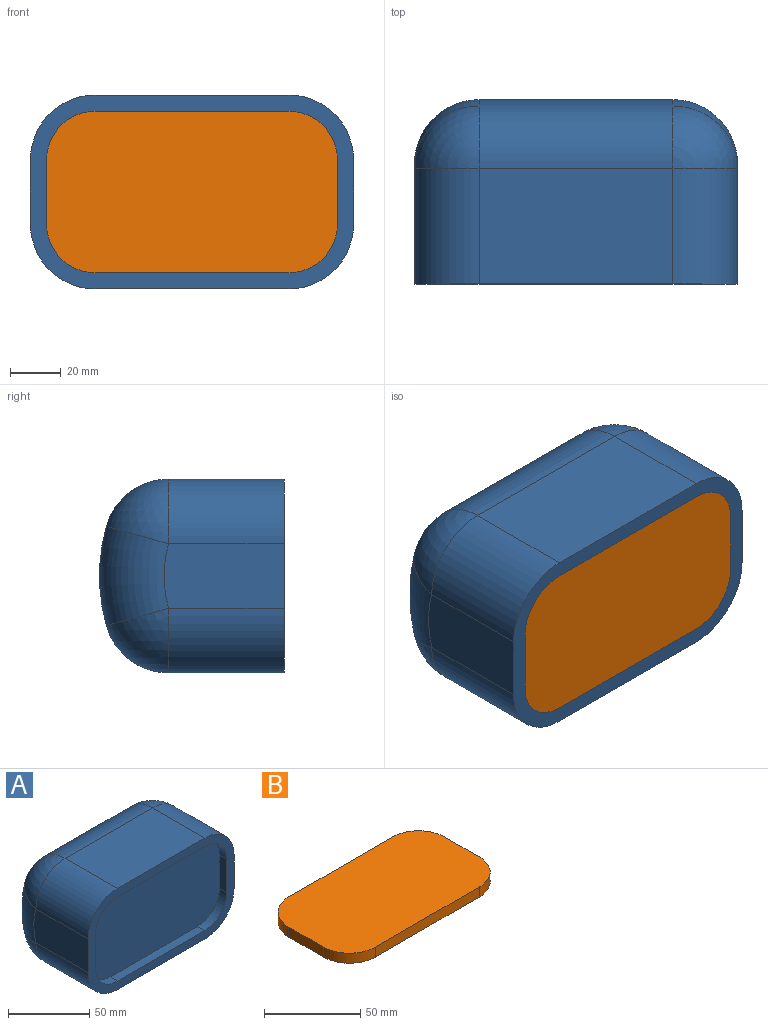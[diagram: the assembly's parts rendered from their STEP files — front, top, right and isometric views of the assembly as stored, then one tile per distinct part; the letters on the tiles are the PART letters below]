
ASSEMBLY  parts=2 mates=1
PART A: 27 faces, bbox 127x78.6x76.2 mm
  f0: plane 127x76.2mm, normal (0,-1,0), area 2177.1mm2, adj f1,f2,f3,f4,f6,f8,f11,f14
  f1: plane 47.23x25.4mm, normal (1,0,0), area 1185mm2, adj f0,f8,f13,f14
  f2: plane 76.2x45.49mm, normal (0,0,1), area 3466.4mm2, adj f0,f11,f14,f17
  f3: plane 47.23x25.4mm, normal (-1,0,0), area 1185mm2, adj f0,f6,f11,f12
  f4: plane 76.2x45.49mm, normal (0,0,-1), area 3466.4mm2, adj f0,f6,f7,f8
  f5: cylinder r=72.63mm len=76.2mm, axis (-1,0,0), area 3013.5mm2, adj f7,f12,f13,f17
  f6: cylinder r=25.4mm len=45.49mm, axis (0,1,0), area 1815mm2, adj f0,f3,f4,f9
  f7: cylinder r=25.4mm len=76.2mm, axis (-1,0,0), area 2513.3mm2, adj f4,f5,f9,f10
  f8: cylinder r=25.4mm len=45.49mm, axis (0,-1,0), area 1815mm2, adj f0,f1,f4,f10
  f9: sphere r=25.4mm, area 837.8mm2, adj f6,f7,f12
  f10: sphere r=25.4mm, area 837.8mm2, adj f7,f8,f13
  f11: cylinder r=25.4mm len=45.49mm, axis (0,-1,0), area 1815mm2, adj f0,f2,f3,f15
  f12: torus R=47.23mm, axis (-1,0,0), area 1377.3mm2, adj f3,f5,f9,f15
  f13: torus R=47.23mm, axis (-1,0,0), area 1377.3mm2, adj f1,f5,f10,f16
  f14: cylinder r=25.4mm len=45.49mm, axis (0,1,0), area 1815mm2, adj f0,f1,f2,f16
  f15: sphere r=25.4mm, area 837.8mm2, adj f11,f12,f17
  f16: sphere r=25.4mm, area 837.8mm2, adj f13,f14,f17
  f17: cylinder r=25.4mm len=76.2mm, axis (-1,0,0), area 2513.3mm2, adj f2,f5,f15,f16
  f18: plane 76.2x6.35mm, normal (0,0,1), area 483.9mm2, adj f0,f19,f25,f26
  f19: cylinder r=19.05mm len=19.05mm, axis (0,-1,0), area 190mm2, adj f0,f18,f20,f26
  f20: plane 25.4x6.35mm, normal (-1,0,0), area 161.3mm2, adj f0,f19,f21,f26
  f21: cylinder r=19.05mm len=19.05mm, axis (0,-1,0), area 190mm2, adj f0,f20,f22,f26
  f22: plane 76.2x6.35mm, normal (0,0,-1), area 483.9mm2, adj f0,f21,f23,f26
  f23: cylinder r=19.05mm len=19.05mm, axis (0,-1,0), area 190mm2, adj f0,f22,f24,f26
  f24: plane 25.4x6.35mm, normal (1,0,0), area 161.3mm2, adj f0,f23,f25,f26
  f25: cylinder r=19.05mm len=19.05mm, axis (0,-1,0), area 190mm2, adj f0,f18,f24,f26
  f26: plane 114.3x63.5mm, normal (0,-1,0), area 6946.5mm2, adj f18,f19,f20,f21,f22,f23,f24,f25
PART B: 10 faces, bbox 114.3x63.5x6.4 mm
  f0: plane 76.2x6.35mm, normal (0,-1,0), area 483.9mm2, adj f1,f7,f8,f9
  f1: cylinder r=19.05mm len=19.05mm, axis (0,0,-1), area 190mm2, adj f0,f2,f8,f9
  f2: plane 25.4x6.35mm, normal (1,0,0), area 161.3mm2, adj f1,f3,f8,f9
  f3: cylinder r=19.05mm len=19.05mm, axis (0,0,-1), area 190mm2, adj f2,f4,f8,f9
  f4: plane 76.2x6.35mm, normal (0,1,0), area 483.9mm2, adj f3,f5,f8,f9
  f5: cylinder r=19.05mm len=19.05mm, axis (0,0,-1), area 190mm2, adj f4,f6,f8,f9
  f6: plane 25.4x6.35mm, normal (-1,0,0), area 161.3mm2, adj f5,f7,f8,f9
  f7: cylinder r=19.05mm len=19.05mm, axis (0,0,-1), area 190mm2, adj f0,f6,f8,f9
  f8: plane 114.3x63.5mm, normal (0,0,1), area 6946.5mm2, adj f0,f1,f2,f3,f4,f5,f6,f7
  f9: plane 114.3x63.5mm, normal (0,0,-1), area 6946.5mm2, adj f0,f1,f2,f3,f4,f5,f6,f7
PLACE A t=(21.6,44.04,-7.84)mm
PLACE B rot(axis=(-1,0,0),90deg) t=(42.79,-32.16,-54.75)mm
MATE fastened B.f8 <-> A.f26  axis (0,1,0) through (21.6,-25.81,-7.84)mm
